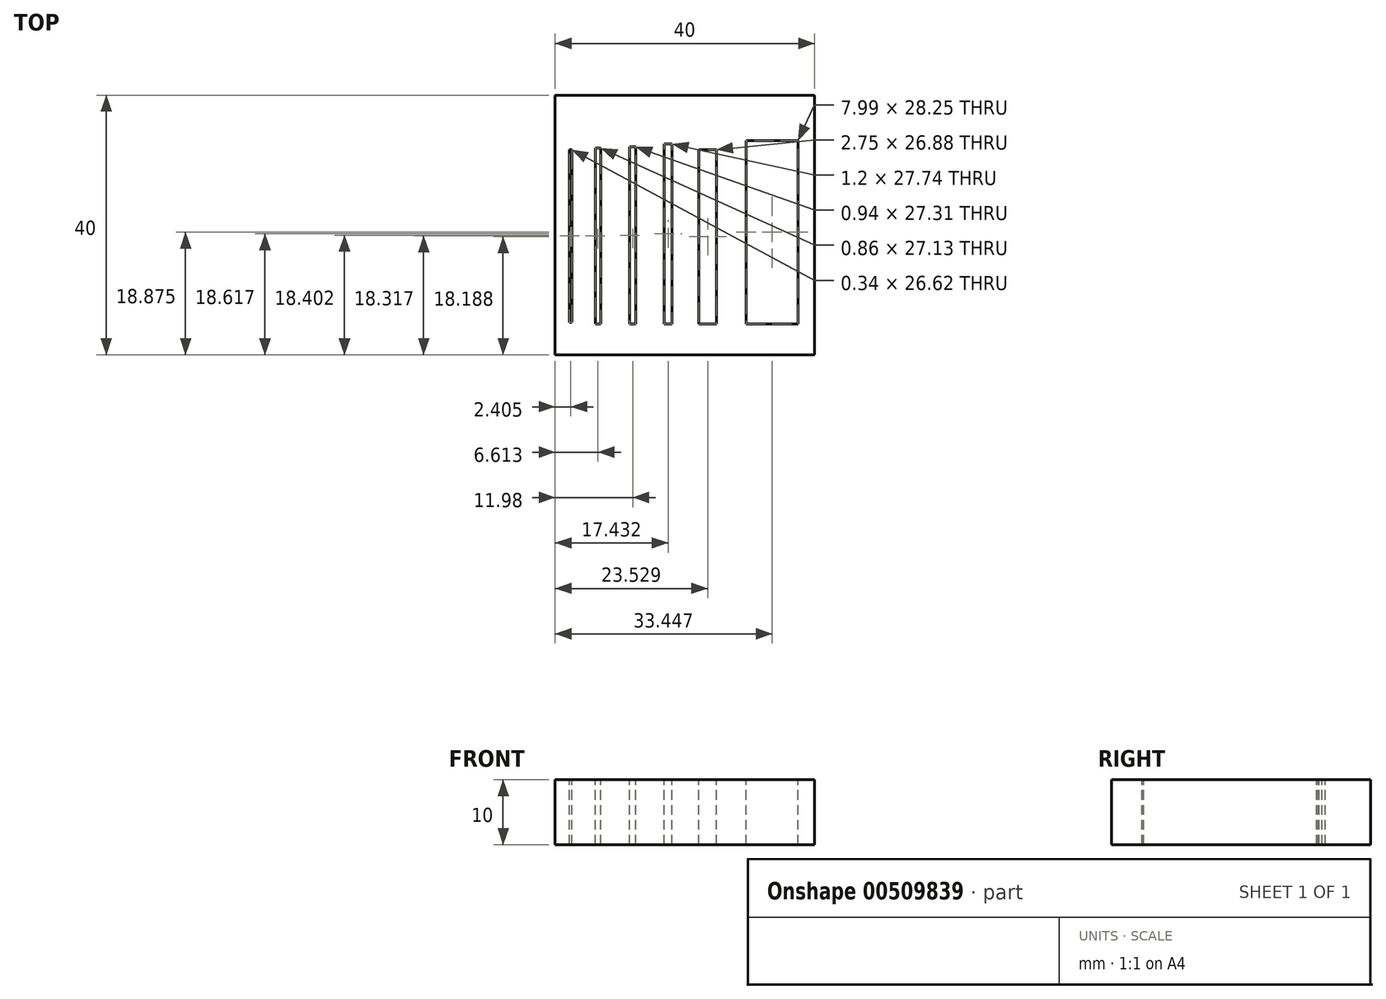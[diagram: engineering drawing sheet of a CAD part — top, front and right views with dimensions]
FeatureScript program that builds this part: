
annotation { "Feature Type Name" : "Feature", "Feature Type Description" : "" }
export const myFeature = defineFeature(function(context is Context, id is Id, definition is map)
    precondition{}
    {
        {
            var Q0;
            Q0=qCreatedBy(makeId("Top.planeOp"),FACE);
            var sketch = newSketch(context, id + "F0", { "sketchPlane" : qUnion([Q0])});
            skLineSegment(sketch, "E0.bottom", {"start": v(20, -20) * mm, "end": v(-20, -20) * mm});
            skLineSegment(sketch, "E0.top", {"start": v(20, 20) * mm, "end": v(-20, 20) * mm});
            skLineSegment(sketch, "E0.left", {"start": v(20, -20) * mm, "end": v(20, 20) * mm});
            skLineSegment(sketch, "E0.right", {"start": v(-20, -20) * mm, "end": v(-20, 20) * mm});
            skPoint(sketch, "E0.middle", {"position": v(0, 0) * mm});
            skSolve(sketch);
        }
        {
            var Q0;
            Q0=makeQuery(id+"F0.imprint","IMPRINT",FACE,{"disambiguationData":[TD([[makeQuery(id+"F0.imprint","IMPRINT",EDGE,{"derivedFrom":sQuery(id+"F0.wireOp",EDGE,"E0.bottom")}),-1.0]])]});
            extrude(context, id + "F1", {"entities" : qUnion([Q0]), "depth" : 10 * mm});
        }
        {
            var Q0;
            Q0=makeQuery(id+"F1.opExtrude","CAP_FACE",FACE,{"disambiguationData":[OSD([sQuery(id+"F0.wireOp",EDGE,"E0.bottom"),sQuery(id+"F0.wireOp",EDGE,"E0.top"),sQuery(id+"F0.wireOp",EDGE,"E0.left"),sQuery(id+"F0.wireOp",EDGE,"E0.right")])],"isStart":false});
            var sketch = newSketch(context, id + "F2", { "sketchPlane" : qUnion([Q0])});
            skLineSegment(sketch, "E1.bottom", {"start": v(-17.77, 11.63) * mm, "end": v(-17.42, 11.63) * mm});
            skLineSegment(sketch, "E1.top", {"start": v(-17.77, -15) * mm, "end": v(-17.42, -15) * mm});
            skLineSegment(sketch, "E1.left", {"start": v(-17.77, 11.63) * mm, "end": v(-17.77, -15) * mm});
            skLineSegment(sketch, "E1.right", {"start": v(-17.42, 11.63) * mm, "end": v(-17.42, -15) * mm});
            skLineSegment(sketch, "E2.bottom", {"start": v(-13.82, 11.88) * mm, "end": v(-12.96, 11.88) * mm});
            skLineSegment(sketch, "E2.top", {"start": v(-13.82, -15.25) * mm, "end": v(-12.96, -15.25) * mm});
            skLineSegment(sketch, "E2.left", {"start": v(-13.82, 11.88) * mm, "end": v(-13.82, -15.25) * mm});
            skLineSegment(sketch, "E2.right", {"start": v(-12.96, 11.88) * mm, "end": v(-12.96, -15.25) * mm});
            skLineSegment(sketch, "E3.bottom", {"start": v(-8.5, 12.06) * mm, "end": v(-7.55, 12.06) * mm});
            skLineSegment(sketch, "E3.top", {"start": v(-8.5, -15.25) * mm, "end": v(-7.55, -15.25) * mm});
            skLineSegment(sketch, "E3.left", {"start": v(-8.5, 12.06) * mm, "end": v(-8.5, -15.25) * mm});
            skLineSegment(sketch, "E3.right", {"start": v(-7.55, 12.06) * mm, "end": v(-7.55, -15.25) * mm});
            skLineSegment(sketch, "E4.bottom", {"start": v(-3.17, 12.48) * mm, "end": v(-1.97, 12.48) * mm});
            skLineSegment(sketch, "E4.top", {"start": v(-3.17, -15.25) * mm, "end": v(-1.97, -15.25) * mm});
            skLineSegment(sketch, "E4.left", {"start": v(-3.17, 12.48) * mm, "end": v(-3.17, -15.25) * mm});
            skLineSegment(sketch, "E4.right", {"start": v(-1.97, 12.48) * mm, "end": v(-1.97, -15.25) * mm});
            skLineSegment(sketch, "E5.bottom", {"start": v(2.15, 11.63) * mm, "end": v(4.9, 11.63) * mm});
            skLineSegment(sketch, "E5.top", {"start": v(2.15, -15.25) * mm, "end": v(4.9, -15.25) * mm});
            skLineSegment(sketch, "E5.left", {"start": v(2.15, 11.63) * mm, "end": v(2.15, -15.25) * mm});
            skLineSegment(sketch, "E5.right", {"start": v(4.9, 11.63) * mm, "end": v(4.9, -15.25) * mm});
            skLineSegment(sketch, "E6.bottom", {"start": v(9.45, 13) * mm, "end": v(17.44, 13) * mm});
            skLineSegment(sketch, "E6.top", {"start": v(9.45, -15.25) * mm, "end": v(17.44, -15.25) * mm});
            skLineSegment(sketch, "E6.left", {"start": v(9.45, 13) * mm, "end": v(9.45, -15.25) * mm});
            skLineSegment(sketch, "E6.right", {"start": v(17.44, 13) * mm, "end": v(17.44, -15.25) * mm});
            skSolve(sketch);
        }
        {
            var Q0;
            Q0 = qSketchRegion(id + "F2", true);
            extrude(context, id + "F3", {"entities" : qUnion([Q0]), "operationType" : NewBodyOperationType.REMOVE, "oppositeDirection" : true, "depth" : 25 * mm});
        }
    });
